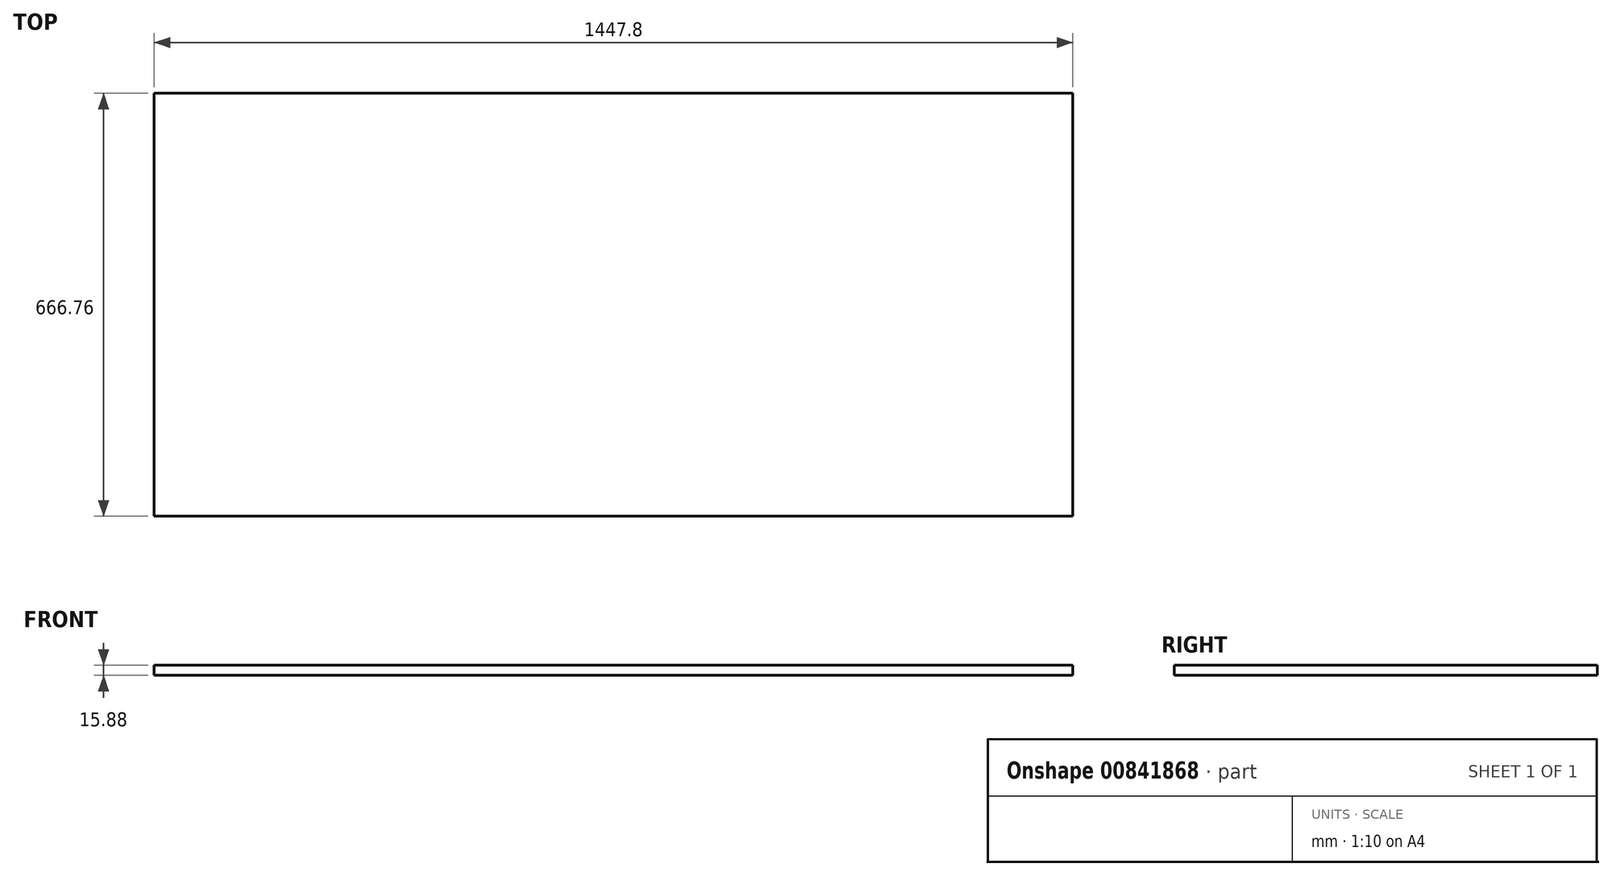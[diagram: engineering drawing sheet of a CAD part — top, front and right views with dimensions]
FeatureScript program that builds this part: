
annotation { "Feature Type Name" : "Feature", "Feature Type Description" : "" }
export const myFeature = defineFeature(function(context is Context, id is Id, definition is map)
    precondition{}
    {
        {
            var Q0;
            Q0=qCreatedBy(makeId("Top.planeOp"),FACE);
            var sketch = newSketch(context, id + "F0", { "sketchPlane" : qUnion([Q0])});
            skLineSegment(sketch, "E0.bottom", {"start": v(723.9, 333.38) * mm, "end": v(-723.9, 333.38) * mm});
            skLineSegment(sketch, "E0.top", {"start": v(723.9, -333.38) * mm, "end": v(-723.9, -333.38) * mm});
            skLineSegment(sketch, "E0.left", {"start": v(723.9, 333.38) * mm, "end": v(723.9, -333.38) * mm});
            skLineSegment(sketch, "E0.right", {"start": v(-723.9, 333.38) * mm, "end": v(-723.9, -333.38) * mm});
            skPoint(sketch, "E0.middle", {"position": v(0, 0) * mm});
            skSolve(sketch);
        }
        {
            var Q0;
            Q0 = qSketchRegion(id + "F0", true);
            extrude(context, id + "F1", {"entities" : qUnion([Q0]), "depth" : 15.88 * mm, "offsetDistance" : 25.4 * mm});
        }
    });
